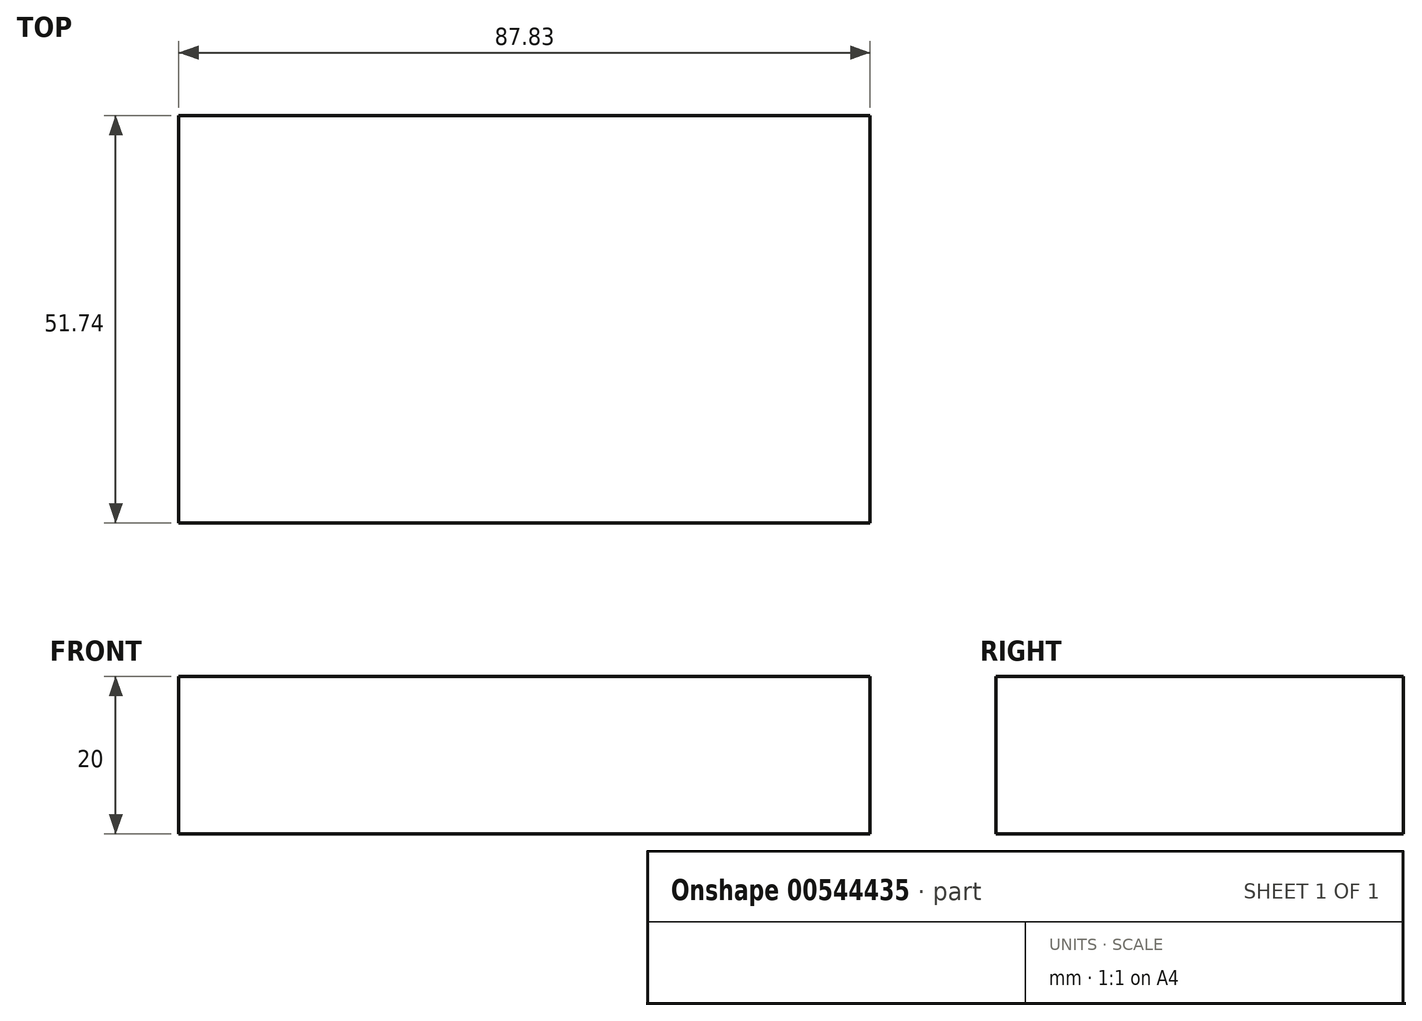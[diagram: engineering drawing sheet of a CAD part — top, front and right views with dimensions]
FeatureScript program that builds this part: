
annotation { "Feature Type Name" : "Feature", "Feature Type Description" : "" }
export const myFeature = defineFeature(function(context is Context, id is Id, definition is map)
    precondition{}
    {
        {
            var Q0;
            Q0=qCreatedBy(makeId("Top.planeOp"),FACE);
            var sketch = newSketch(context, id + "F0", { "sketchPlane" : qUnion([Q0])});
            skLineSegment(sketch, "E0.bottom", {"start": v(41.2, 25.87) * mm, "end": v(-46.62, 25.87) * mm});
            skLineSegment(sketch, "E0.top", {"start": v(41.2, -25.87) * mm, "end": v(-46.62, -25.87) * mm});
            skLineSegment(sketch, "E0.left", {"start": v(41.2, 25.87) * mm, "end": v(41.2, -25.87) * mm});
            skLineSegment(sketch, "E0.right", {"start": v(-46.62, 25.87) * mm, "end": v(-46.62, -25.87) * mm});
            skPoint(sketch, "E0.middle", {"position": v(-2.7, 0) * mm});
            skSolve(sketch);
        }
        {
            var Q0;
            Q0=makeQuery(id+"F0.imprint","IMPRINT",FACE,{"disambiguationData":[TD([[makeQuery(id+"F0.imprint","IMPRINT",EDGE,{"derivedFrom":sQuery(id+"F0.wireOp",EDGE,"E0.bottom")}),1.0]])]});
            extrude(context, id + "F1", {"entities" : qUnion([Q0]), "depth" : 20 * mm, "offsetDistance" : 25.4 * mm});
        }
    });
